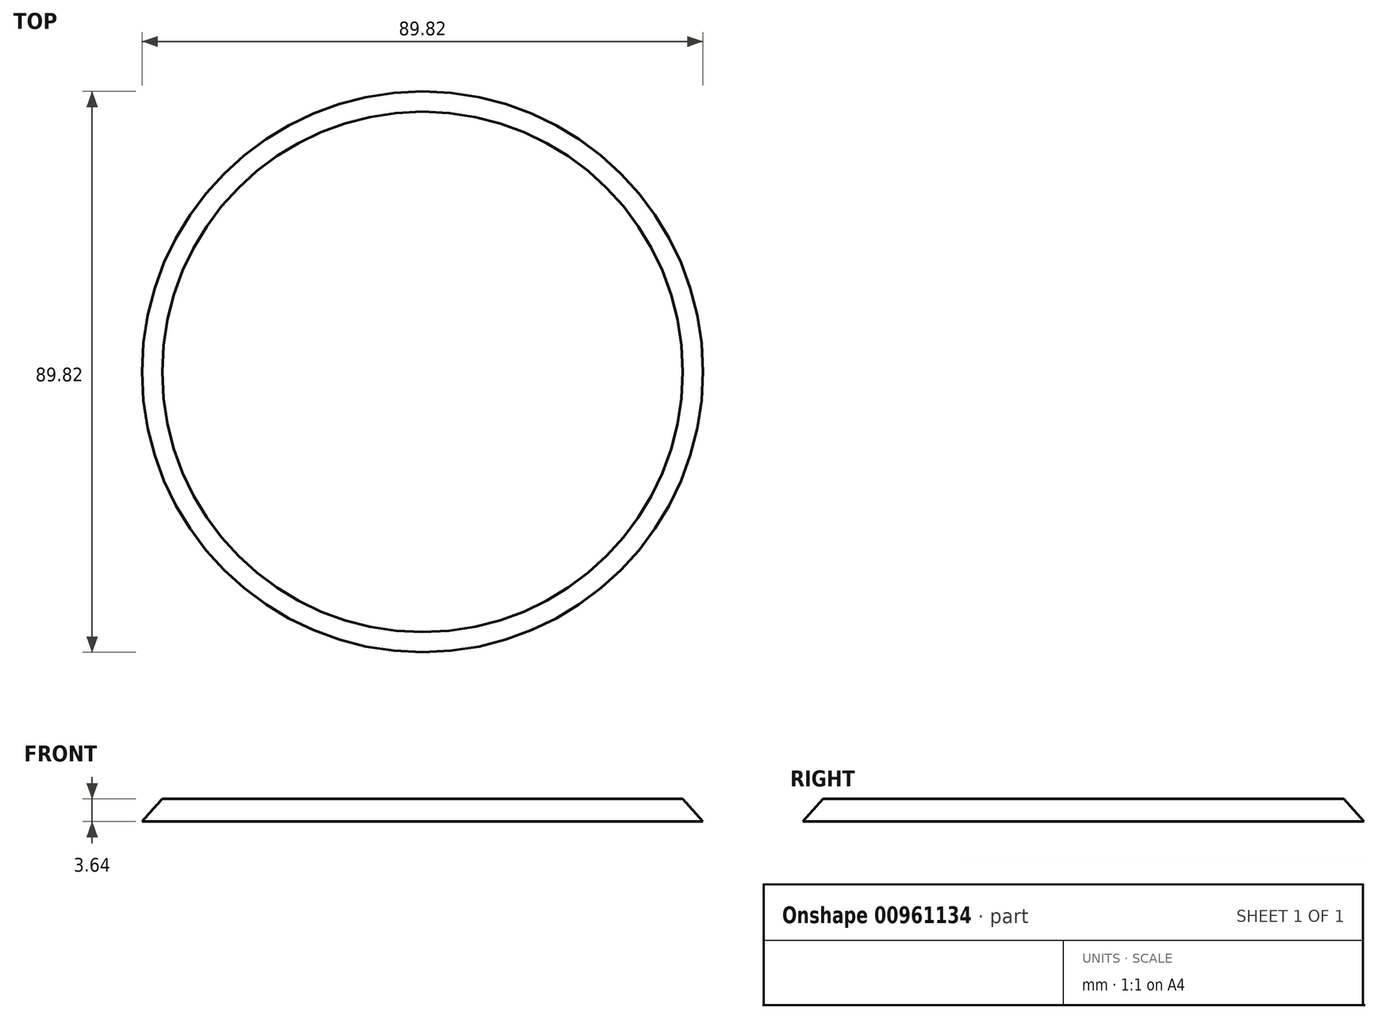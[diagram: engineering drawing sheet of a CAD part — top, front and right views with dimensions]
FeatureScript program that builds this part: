
annotation { "Feature Type Name" : "Feature", "Feature Type Description" : "" }
export const myFeature = defineFeature(function(context is Context, id is Id, definition is map)
    precondition{}
    {
        {
            var Q0;
            Q0=qCreatedBy(makeId("Front.planeOp"),FACE);
            var sketch = newSketch(context, id + "F0", { "sketchPlane" : qUnion([Q0])});
            skLineSegment(sketch, "E0", {"start": v(0, 20.49) * mm, "end": v(41.68, 20.49) * mm});
            skLineSegment(sketch, "E1", {"start": v(41.68, 20.49) * mm, "end": v(44.91, 16.85) * mm});
            skLineSegment(sketch, "E2", {"start": v(44.91, 16.85) * mm, "end": v(0, 16.85) * mm});
            skLineSegment(sketch, "E3", {"start": v(0, 16.85) * mm, "end": v(0, 20.49) * mm});
            skSolve(sketch);
        }
        {
            var Q0;
            Q0=makeQuery(id+"F0.imprint","IMPRINT",FACE,{"disambiguationData":[TD([[makeQuery(id+"F0.imprint","IMPRINT",EDGE,{"derivedFrom":sQuery(id+"F0.wireOp",EDGE,"E0")}),-1.0]])]});
            var Q1;
            Q1=sQuery(id+"F0.wireOp",EDGE,"E3");
            revolve(context, id + "F1", {"surfaceOperationType" : NewSurfaceOperationType.NEW, "entities" : qUnion([Q0]), "axis" : qUnion([Q1]), "revolveType" : RevolveType.FULL});
        }
    });
